# Revit family: Sanitary_Wash-Basins_hansgrohe_22410CHN-CubeStack-Furniture-washbasin-8_1
name_source: partatom
category: Plumbing Fixtures
revit_build: Autodesk Revit 2018 (Build: 20170223_1515(x64)
units: mm (PartAtom-declared; Revit-internal decimal feet)

## family parameters
Always vertical = No
Cut with Voids When Loaded = No
OmniClass Number = 23.45.05.14.14
OmniClass Title = Sinks/Lavatories
Part Type = Normal
Room Calculation Point = No
Round Connector Dimension = Use Diameter
Shared = No
Work Plane-Based = Yes

## types (1)
- 007 White
    Always visible = Yes
    BIMobject category = Wash Basins
    Default Elevation = 1219.2 mm  [stored 4 ft]
    Description = CubeStack Furniture washbasin 800/500
    Design country = Germany
    EAN code = 4059625299784
    Edition number = 1
    GTIN code = https://4059625299784
    IFC Classification = Sanitary Terminal
    Manufacturer = hansgrohe
    Manufacturer country = Germany
    Manufacturer name = hansgrohe
    Masterformat 2014 Code = 22 41 16.16
    Masterformat 2014 Description = Residential Sinks
    Material 1 = Hansgrohe - Metal - Graphite
    Material 2 = Hansgrohe - Plastic - Gray
    Material 3 = Hansgrohe - Steel enamel - White
    Material 4 = Hansgrohe - Plastic - Mat White
    Model = 22410CHN
    NBS Reference Code = 31-79
    NBS Reference Description = Sinks, Wash Basins And Troughs
    OmniClass Code = 23-31 13 00
    OmniClass Description = Sinks
    Product Guid = ee32671c-22e2-476b-b398-6ef7400a213b
    Product SKU = 22410CHN
    Product data url = https://bimobject.com
    Product family = CubeStack
    Product group = Washbasins
    Product name = 22410CHN CubeStack Furniture washbasin 800/500
    QR code = https://bimobject.com
    UNSPSC Code = 30181504
    URL = https://www.hansgrohe.com
    Uniclass 2015 Code = Pr_40_20_96
    Uniclass 2015 Name = Wash basins, sinks and troughs
    Uniformat II Code = D2010
    Uniformat II Description = Plumbing Fixtures
    Water Outlet = 47 mm  [stored 0.154199 ft]
    Weight Net (Kg) = 15.5

note: [stored X ft] marks values corroborated as IEEE doubles in the binary element streams (Revit-internal decimal feet)

## geometry (parser evidence)
native form markers: Sweep x2
no freeform markers — native parametric forms only
